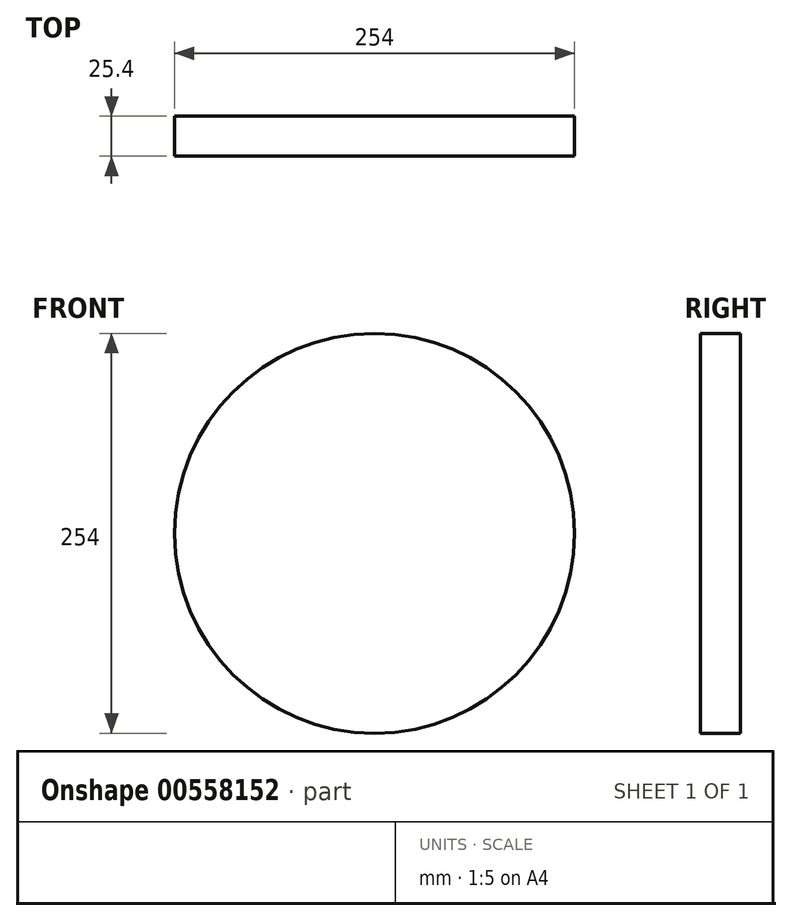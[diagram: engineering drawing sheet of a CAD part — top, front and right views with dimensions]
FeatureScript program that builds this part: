
annotation { "Feature Type Name" : "Feature", "Feature Type Description" : "" }
export const myFeature = defineFeature(function(context is Context, id is Id, definition is map)
    precondition{}
    {
        {
            var Q0;
            Q0=qCreatedBy(makeId("Front.planeOp"),FACE);
            var sketch = newSketch(context, id + "F0", { "sketchPlane" : qUnion([Q0])});
            skCircle(sketch, "E0", {"center": v(0, 0) * mm, "radius": 127 * mm});
            skSolve(sketch);
        }
        {
            var Q0;
            Q0 = qSketchRegion(id + "F0", true);
            extrude(context, id + "F1", {"entities" : qUnion([Q0]), "depth" : 25.4 * mm, "offsetDistance" : 25.4 * mm});
        }
    });
